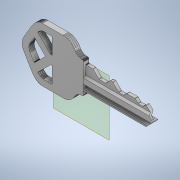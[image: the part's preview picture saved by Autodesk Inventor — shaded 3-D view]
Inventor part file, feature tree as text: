
AUTODESK INVENTOR PART (.ipt)
format: ipt  version: 2020 (Build 240168000, 168)  size: 1,432,064 bytes
history: native  units: in
note: dims shown in document units (in); Inventor stores cm internally (conversion verified against a paired STEP export)
features: other x3, fillet x2, projected_geometry x2, plane x1, extrude x1, sketch x1
ambient origin geometry x8: Origin, YZ Plane, XZ Plane, XY Plane, X Axis, Y Axis, Z Axis, Center Point
bodies: Solid1 (feature_tree)
feature tree (10):
  other  "KW1_Key_Blank"
  plane  "Work Plane1"
  other  "MeshFeature1"
  extrude  "Extrusion1"  Depth=0.214in
  fillet  "Fillet1"  Radius=0.26in
  fillet  "Fillet2"  Radius=0.214in
  sketch  "Sketch2"  dims[d72=135.0deg d84=0.214in d85=0.26in d86=0.214in d87=0.306in d88=0.237in d89=0.26in d90=0.256in d91=0.547in d92=0.397in d93=0.697in d94=0.847in d108=1.0in d109=0.0in d110=0.01in d111=0.03in]
  other  "Image5"
  projected_geometry  "Projected Loop1"
  projected_geometry  "Projected Loop2"
